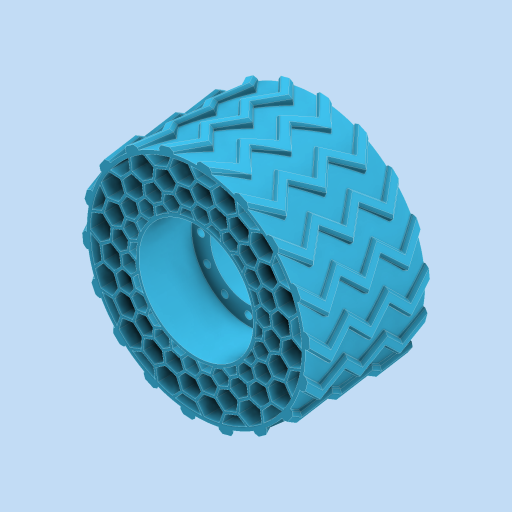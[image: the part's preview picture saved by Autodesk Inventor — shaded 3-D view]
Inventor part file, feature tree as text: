
AUTODESK INVENTOR PART (.ipt)
format: ipt  version: 2023 (Build 270158000, 158)  size: 1,241,600 bytes
history: native  units: in
note: dims shown in document units (in); Inventor stores cm internally (conversion verified against a paired STEP export)
features: extrude x21, other x18, thicken_offset x17, sketch x5, pattern_circular x2, plane x2, mirror x1, sweep x1
ambient origin geometry x8: Origin, YZ Plane, XZ Plane, XY Plane, X Axis, Y Axis, Z Axis, Center Point
bodies: Solid1 (feature_tree)
feature tree (67):
  sketch  "Sketch1"  dims[d0=3.1496in d1=0.0in d2=3.1496in d3=0.0in]
  extrude  "Extrusion1"  Depth=3.1496in TaperAngle=0.0deg
  thicken_offset  "Thicken1"
  thicken_offset  "Thicken2"
  thicken_offset  "Thicken3"
  thicken_offset  "Thicken4"
  thicken_offset  "Thicken5"
  thicken_offset  "Thicken6"
  thicken_offset  "Thicken7"
  thicken_offset  "Thicken8"
  thicken_offset  "Thicken9"
  thicken_offset  "Thicken10"
  thicken_offset  "Thicken11"
  thicken_offset  "Thicken12"
  thicken_offset  "Thicken13"
  thicken_offset  "Thicken14"
  thicken_offset  "Thicken15"
  thicken_offset  "Thicken16"
  thicken_offset  "Thicken17"
  pattern_circular  "Circular Pattern1"  Count=8  [1 undecoded]
  sketch  "Sketch2"  dims[d4=0.0945in d5=3.1496in d6=0.0in]
  extrude  "Extrusion2"  Depth=3.1496in TaperAngle=0.0deg
  plane  "Work Plane1"
  mirror  "Mirror1"
  extrude  "Extrusion3"  Depth=3.1496in TaperAngle=0.0deg
  sketch  "Sketch3"  dims[d7=0.063in d8=3.1496in d9=0.0in]
  other  "Work Point1"
  plane  "Work Plane2"
  sweep  "Sweep1"
  extrude  "Extrusion4"  Depth=0.063in
  pattern_circular  "Circular Pattern2"  Count=8  [1 undecoded]
  other  "Srf1"
  other  "Srf2"
  other  "Srf3"
  other  "Srf4"
  other  "Srf5"
  other  "Srf6"
  other  "Srf7"
  other  "Srf8"
  other  "Srf9"
  other  "Srf10"
  other  "Srf11"
  other  "Srf12"
  other  "Srf13"
  other  "Srf14"
  other  "Srf15"
  other  "Srf16"
  other  "Srf17"
  sketch  "Sketch4"  dims[d10=0.063in d11=3.1496in d12=0.0in]
  sketch  "Sketch5"  dims[d13=0.063in d14=3.1496in d15=0.0in d16=0.063in d17=3.1496in d18=0.0in d19=0.063in d20=3.1496in d21=0.0in d22=0.063in d23=3.1496in d24=0.0in d25=0.063in d26=3.1496in d27=0.0in d28=0.063in d29=3.1496in d30=0.0in d31=0.063in d32=3.1496in d33=0.0in d34=0.063in d35=3.1496in d36=0.0in d37=0.063in d38=3.1496in d39=0.0in d40=0.063in d41=3.1496in d42=0.0in d43=0.063in d44=3.1496in d45=0.0in d46=0.063in d47=3.1496in d48=0.0in d49=0.063in d50=3.1496in d51=0.0in d52=0.063in d53=5.5118in d54=360.0deg d57=2.5in d58=0.19in d59=4.7244in d61=360.0deg d63=1.378in d64=0.0in d65=0.5in d66=0.0in d67=0.0in d68=0.002in d69=0.3937in d70=0.126in d71=0.0787in d72=0.0787in d73=0.0787in d74=0.0787in d75=0.0in d76=0.0in d77=0.0in d78=0.0in d79=7.0866in d80=360.0deg d82=3.0in d83=0.5in]
  extrude  "ExtrusionSrf1"  Depth=0.063in
  extrude  "ExtrusionSrf2"  Depth=3.1496in TaperAngle=0.0deg
  extrude  "ExtrusionSrf3"  Depth=0.063in
  extrude  "ExtrusionSrf4"  Depth=3.1496in TaperAngle=0.0deg
  extrude  "ExtrusionSrf5"  Depth=0.063in
  extrude  "ExtrusionSrf6"  Depth=3.1496in TaperAngle=0.0deg
  extrude  "ExtrusionSrf7"  Depth=0.063in
  extrude  "ExtrusionSrf8"  Depth=3.1496in TaperAngle=0.0deg
  extrude  "ExtrusionSrf9"  Depth=0.063in
  extrude  "ExtrusionSrf10"  Depth=3.1496in TaperAngle=0.0deg
  extrude  "ExtrusionSrf11"  Depth=0.063in
  extrude  "ExtrusionSrf12"  Depth=3.1496in TaperAngle=0.0deg
  extrude  "ExtrusionSrf13"  Depth=0.063in
  extrude  "ExtrusionSrf14"  Depth=3.1496in TaperAngle=0.0deg
  extrude  "ExtrusionSrf15"  Depth=0.063in
  extrude  "ExtrusionSrf16"  Depth=3.1496in TaperAngle=0.0deg
  extrude  "ExtrusionSrf17"  Depth=0.063in
note: 2 required parameter values undecoded (feature->parameter linkage not recoverable at this tier; creation-order binding heuristic only, values carry confidence <= 0.55)
